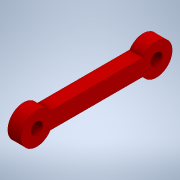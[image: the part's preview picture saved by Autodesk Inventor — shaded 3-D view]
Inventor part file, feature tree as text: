
AUTODESK INVENTOR PART (.ipt)
format: ipt  version: 2020 (Build 240168000, 168)  size: 136,192 bytes
history: native  units: in
note: dims shown in document units (in); Inventor stores cm internally (conversion verified against a paired STEP export)
features: extrude x1, sketch x1
ambient origin geometry x8: Origin, YZ Plane, XZ Plane, XY Plane, X Axis, Y Axis, Z Axis, Center Point
bodies: Solid1 (feature_tree)
feature tree (2):
  extrude  "Extrusion1"  Depth=1.4173in
  sketch  "Sketch1"  dims[d0=0.1378in d1=1.4173in d2=0.1181in d3=0.1181in d4=0.1969in d5=0.1575in d6=0.0in]
